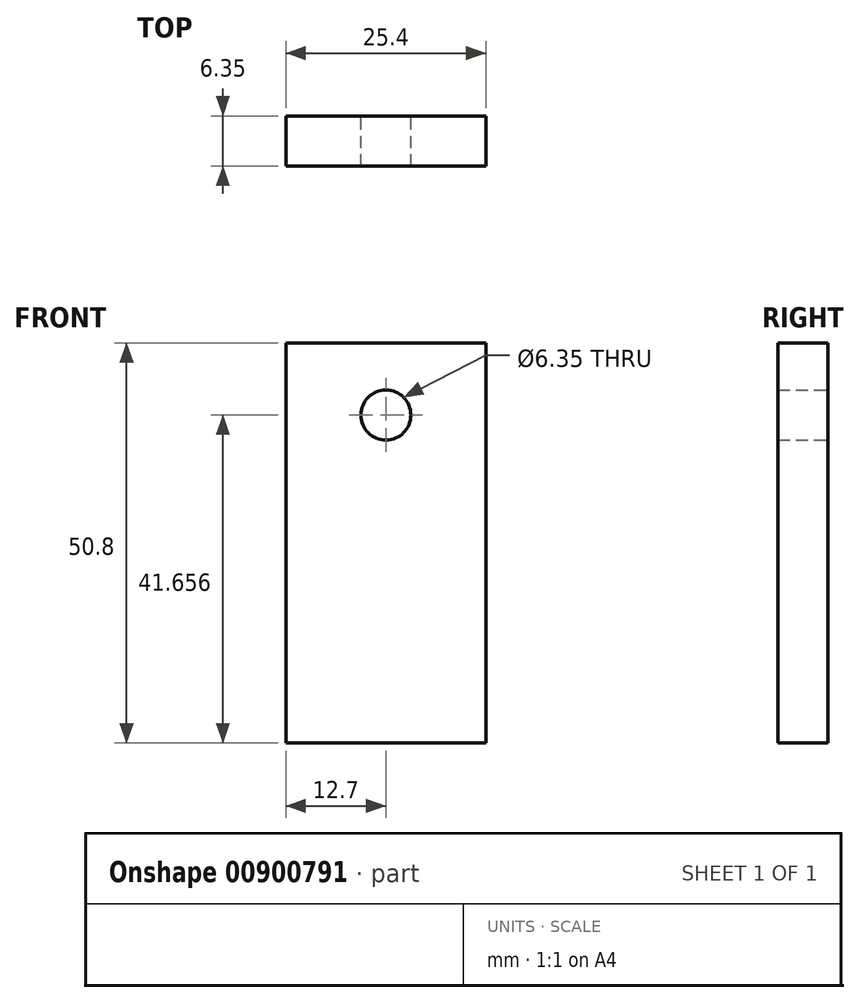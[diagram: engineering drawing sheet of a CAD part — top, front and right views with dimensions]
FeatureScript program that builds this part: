
annotation { "Feature Type Name" : "Feature", "Feature Type Description" : "" }
export const myFeature = defineFeature(function(context is Context, id is Id, definition is map)
    precondition{}
    {
        {
            var Q0;
            Q0=qCreatedBy(makeId("Front.planeOp"),FACE);
            var sketch = newSketch(context, id + "F0", { "sketchPlane" : qUnion([Q0])});
            skLineSegment(sketch, "E0.bottom", {"start": v(0, 0) * mm, "end": v(25.4, 0) * mm});
            skLineSegment(sketch, "E0.top", {"start": v(0, 50.8) * mm, "end": v(25.4, 50.8) * mm});
            skLineSegment(sketch, "E0.left", {"start": v(0, 0) * mm, "end": v(0, 50.8) * mm});
            skLineSegment(sketch, "E0.right", {"start": v(25.4, 0) * mm, "end": v(25.4, 50.8) * mm});
            skCircle(sketch, "E1", {"center": v(12.7, 41.66) * mm, "radius": 3.18 * mm});
            skSolve(sketch);
        }
        {
            var Q0;
            Q0=makeQuery(id+"F0.imprint","IMPRINT",FACE,{"disambiguationData":[TD([[makeQuery(id+"F0.imprint","IMPRINT",EDGE,{"derivedFrom":sQuery(id+"F0.wireOp",EDGE,"E0.bottom")}),1.0]])]});
            extrude(context, id + "F1", {"entities" : qUnion([Q0]), "depth" : 6.35 * mm, "offsetDistance" : 25.4 * mm});
        }
    });
